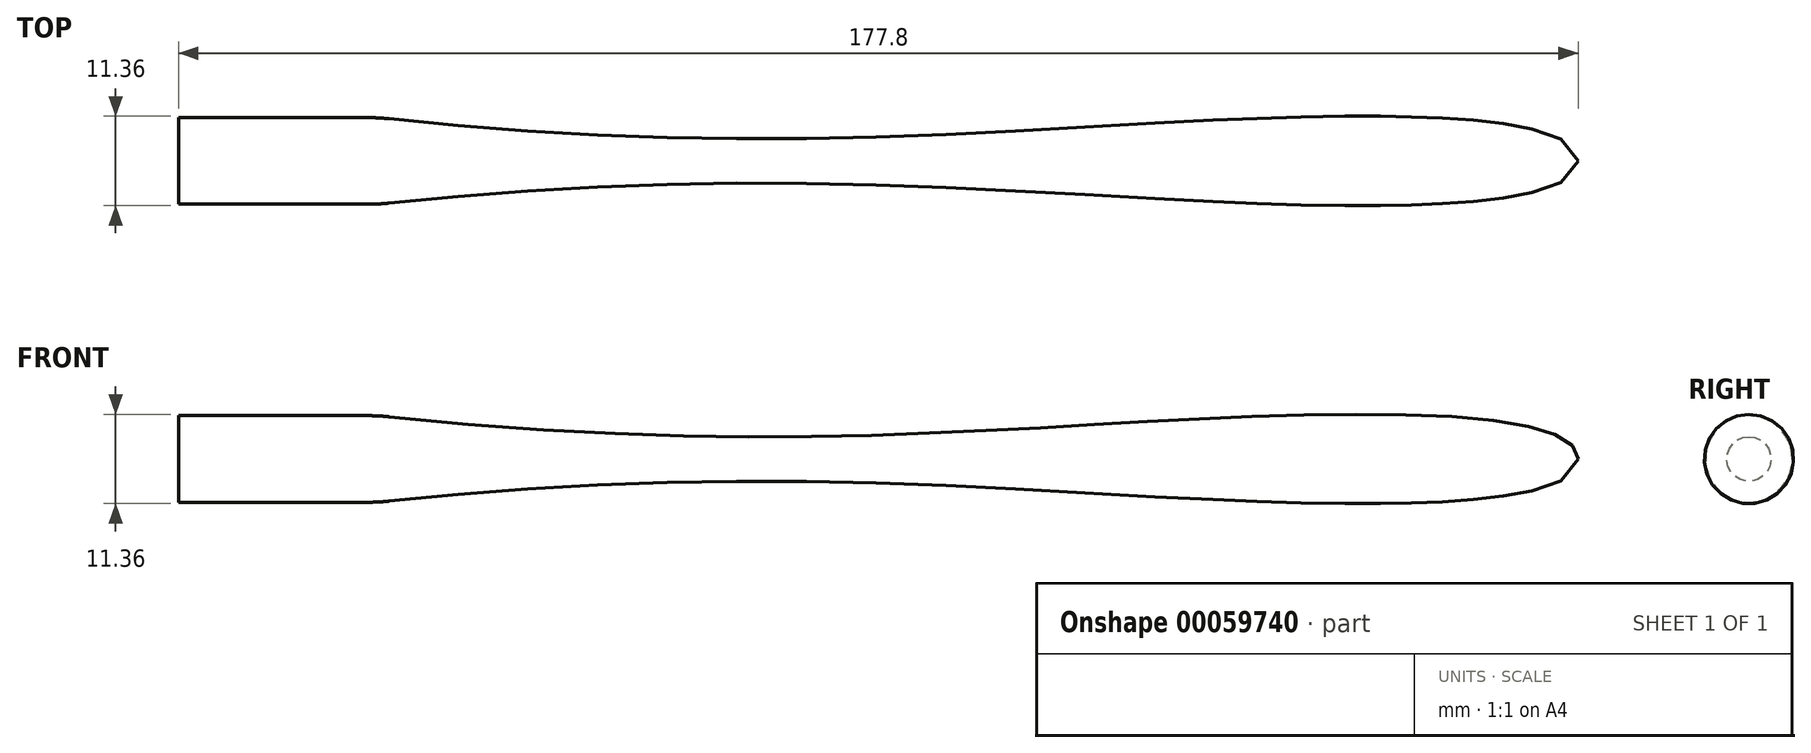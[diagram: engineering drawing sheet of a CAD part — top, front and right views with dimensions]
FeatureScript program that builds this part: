
annotation { "Feature Type Name" : "Feature", "Feature Type Description" : "" }
export const myFeature = defineFeature(function(context is Context, id is Id, definition is map)
    precondition{}
    {
        {
            var Q0;
            Q0=qCreatedBy(makeId("Front.planeOp"),FACE);
            var sketch = newSketch(context, id + "F0", { "sketchPlane" : qUnion([Q0])});
            skLineSegment(sketch, "E0", {"start": v(0, 0) * mm, "end": v(0, 5.5) * mm});
            skLineSegment(sketch, "E1", {"start": v(0, 5.5) * mm, "end": v(24.05, 5.5) * mm});
            skLineSegment(sketch, "E2", {"start": v(0, 0) * mm, "end": v(177.8, 0) * mm, "construction": true});
            skLineSegment(sketch, "E3", {"start": v(177.8, 0) * mm, "end": v(0, 0) * mm});
            skFitSpline(sketch, "E4", {"points": [v(25.4, 5.5) * mm, v(139.7, 5.5) * mm, v(177.8, 0) * mm], "startDerivative": vector(240.84, -26.08) * mm, "endDerivative": vector(0, -44.93) * mm});
            skArc(sketch, "E5.filletArc", {"start": v(26.71, 5.36) * mm, "mid": v(25.38, 5.46) * mm, "end": v(24.05, 5.5) * mm});
            skSolve(sketch);
        }
        {
            var Q0;
            Q0=qSketchRegion(id+"F0",true);
            var Q1;
            Q1=sQuery(id+"F0.wireOp",EDGE,"E3");
            revolve(context, id + "F1", {"entities" : qUnion([Q0]), "axis" : qUnion([Q1]), "revolveType" : RevolveType.FULL});
        }
    });
